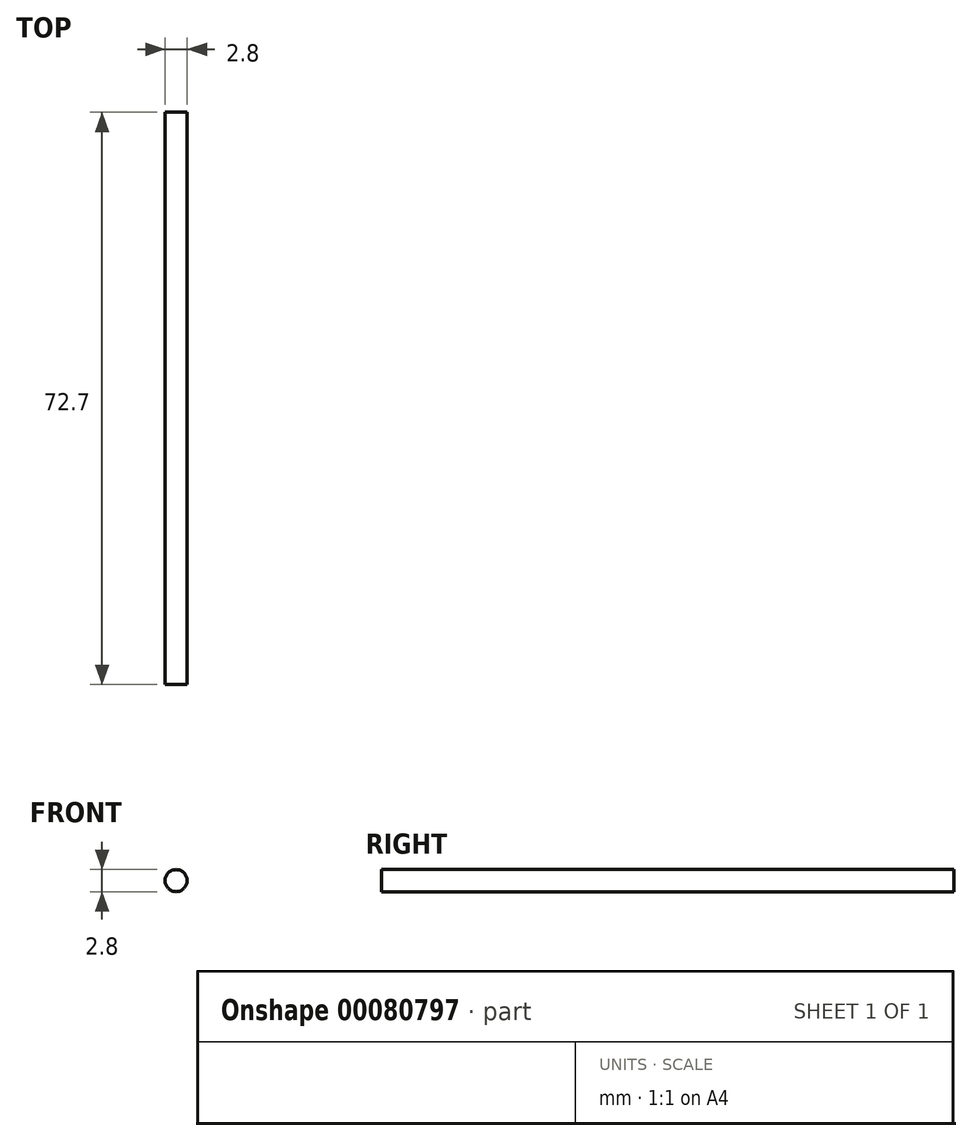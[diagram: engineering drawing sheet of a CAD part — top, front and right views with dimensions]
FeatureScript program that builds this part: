
annotation { "Feature Type Name" : "Feature", "Feature Type Description" : "" }
export const myFeature = defineFeature(function(context is Context, id is Id, definition is map)
    precondition{}
    {
        {
            var Q0;
            Q0=qCreatedBy(makeId("Front.planeOp"),FACE);
            var sketch = newSketch(context, id + "F0", { "sketchPlane" : qUnion([Q0])});
            skCircle(sketch, "E0", {"center": v(0, 0) * mm, "radius": 1.4 * mm});
            skSolve(sketch);
        }
        {
            var Q0;
            Q0 = qSketchRegion(id + "F0", true);
            extrude(context, id + "F1", {"entities" : qUnion([Q0]), "depth" : 72.7 * mm});
        }
    });
